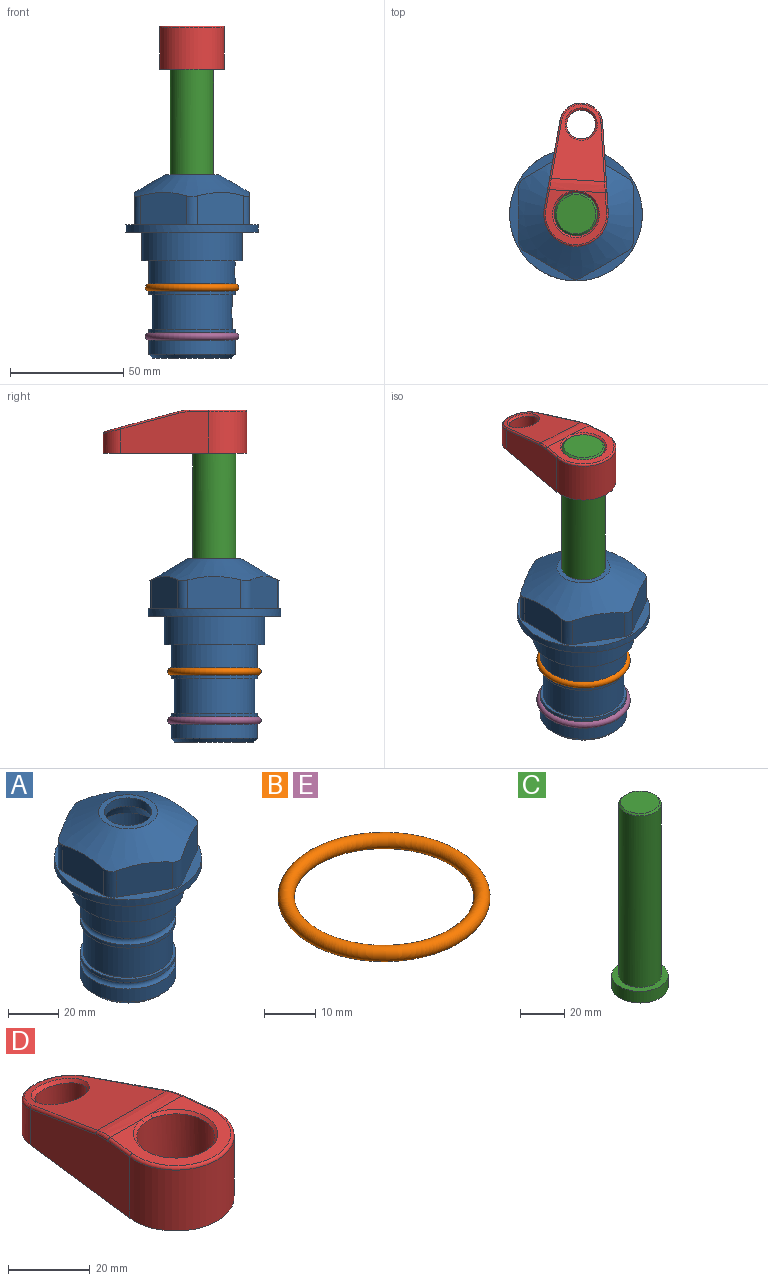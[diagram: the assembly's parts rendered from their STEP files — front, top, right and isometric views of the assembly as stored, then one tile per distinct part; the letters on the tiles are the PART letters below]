
ASSEMBLY  parts=5 mates=4
PART A: 36 faces, bbox 58.7x58.7x81 mm
  f0: cylinder r=17.78mm len=35.56mm, axis (0,0,1), area 1670.8mm2, adj f23,f24,f31
  f1: cylinder r=19.05mm len=38.1mm, axis (0,0,1), area 1191.9mm2, adj f26,f27,f30
  f2: plane 58.66x58.66mm, normal (0,0,-1), area 1150.6mm2, adj f3,f28
  f3: cylinder r=29.33mm len=58.66mm, axis (0,0,-1), area 585.1mm2, adj f2,f4
  f4: plane 58.66x58.66mm, normal (0,0,1), area 475.9mm2, adj f3,f5,f6,f7,f8,f9,f10,f11
  f5: plane 20.32x14.34mm, normal (-0.5,0.87,0), area 324.4mm2, adj f4,f15,f16,f17
  f6: plane 20.32x14.34mm, normal (0.5,0.87,0), area 324.4mm2, adj f4,f14,f15,f17
  f7: plane 23.48x14.34mm, normal (1,0,0), area 324.4mm2, adj f4,f13,f14,f17
  f8: plane 20.32x14.34mm, normal (0.5,-0.87,0), area 324.4mm2, adj f4,f12,f13,f17
  f9: plane 20.32x14.34mm, normal (-0.5,-0.87,0), area 324.4mm2, adj f4,f11,f12,f17
  f10: plane 23.48x14.34mm, normal (-1,0,0), area 324.4mm2, adj f4,f11,f16,f17
  f11: cylinder r=5.08mm len=12.85mm, axis (0,0,-1), area 67.2mm2, adj f4,f9,f10,f17
  f12: cylinder r=5.08mm len=12.85mm, axis (0,0,-1), area 67.2mm2, adj f4,f8,f9,f17
  f13: cylinder r=5.08mm len=12.85mm, axis (0,0,-1), area 67.2mm2, adj f4,f7,f8,f17
  f14: cylinder r=5.08mm len=12.85mm, axis (0,0,-1), area 67.2mm2, adj f4,f6,f7,f17
  f15: cylinder r=5.08mm len=12.85mm, axis (0,0,-1), area 67.2mm2, adj f4,f5,f6,f17
  f16: cylinder r=5.08mm len=12.85mm, axis (0,0,-1), area 67.2mm2, adj f4,f5,f10,f17
  f17: cone r=11.73mm half-angle=60deg, axis (0,0,-1), area 2071.8mm2, adj f5,f6,f7,f8,f9,f10,f11,f12
  f18: plane 23.46x23.46mm, normal (0,0,1), area 147.4mm2, adj f17,f35
  f19: plane 34.93x34.93mm, normal (0,0,-1), area 958mm2, adj f29
  f20: cylinder r=19.05mm len=38.1mm, axis (0,0,1), area 760.1mm2, adj f21,f29
  f21: torus R=19.05mm, axis (0,0,1), area 565.3mm2, adj f20,f22
  f22: cylinder r=19.05mm len=38.1mm, axis (0,0,1), area 190mm2, adj f21,f23
  f23: plane 38.1x38.1mm, normal (0,0,1), area 146.9mm2, adj f0,f22
  f24: plane 38.1x38.1mm, normal (0,0,-1), area 146.9mm2, adj f0,f25
  f25: cylinder r=19.05mm len=38.1mm, axis (0,0,1), area 190mm2, adj f24,f26
  f26: torus R=19.05mm, axis (0,0,1), area 565.3mm2, adj f1,f25
  f27: plane 44.45x44.45mm, normal (0,0,-1), area 411.7mm2, adj f1,f28
  f28: cylinder r=22.23mm len=44.45mm, axis (0,0,1), area 1773.5mm2, adj f2,f27
  f29: cone r=19.05mm half-angle=45deg, axis (0,0,1), area 257.5mm2, adj f19,f20
  f30: cylinder r=3.17mm len=6.75mm, axis (-1,0,0), area 128mm2, adj f1,f33
  f31: cylinder r=3.17mm len=6.35mm, axis (-1,0,0), area 102.5mm2, adj f0,f33
  f32: plane 25.4x25.4mm, normal (0,0,1), area 506.7mm2, adj f33
  f33: cylinder r=12.7mm len=66.42mm, axis (0,0,-1), area 5236.2mm2, adj f30,f31,f32,f34
  f34: cone r=9.53mm half-angle=30deg, axis (0,0,-1), area 443.4mm2, adj f33,f35
  f35: cylinder r=9.53mm len=19.05mm, axis (0,0,-1), area 240.9mm2, adj f18,f34
PART B: 1 faces, bbox 44.7x44.7x3.2 mm
  f0: torus R=19.05mm, axis (0,0,1), area 1193.9mm2
PART C: 6 faces, bbox 25.4x25.4x101.6 mm
  f0: plane 17.46x17.46mm, normal (0,0,1), area 239.5mm2, adj f5
  f1: plane 25.4x25.4mm, normal (0,0,-1), area 506.7mm2, adj f2
  f2: cylinder r=12.7mm len=25.4mm, axis (0,0,1), area 506.7mm2, adj f1,f3
  f3: plane 25.4x25.4mm, normal (0,0,1), area 221.7mm2, adj f2,f4
  f4: cylinder r=9.53mm len=94.46mm, axis (0,0,1), area 5653mm2, adj f3,f5
  f5: cone r=8.73mm half-angle=45deg, axis (0,0,-1), area 64.4mm2, adj f0,f4
PART D: 31 faces, bbox 31.7x65.5x19.8 mm
  f0: plane 39.12x18.26mm, normal (0.99,0.12,0), area 612.2mm2, adj f1,f4,f7,f11,f13,f15
  f1: cylinder r=9.53mm len=18.91mm, axis (0,0,-1), area 296.1mm2, adj f0,f2,f7,f17
  f2: plane 39.12x18.26mm, normal (-0.99,0.12,0), area 612.2mm2, adj f1,f4,f7,f12,f14,f16
  f3: cylinder r=6.35mm len=12.7mm, axis (0,0,-1), area 362.4mm2, adj f7,f18
  f4: cylinder r=14.29mm len=28.58mm, axis (0,0,-1), area 882.2mm2, adj f0,f2,f7,f10
  f5: cylinder r=9.53mm len=19.05mm, axis (0,0,-1), area 1092.6mm2, adj f7,f19,f20
  f6: plane 26.99x23.69mm, normal (0,0,1), area 216.2mm2, adj f9,f10,f11,f12,f19
  f7: plane 63.5x28.58mm, normal (0,0,-1), area 661.8mm2, adj f0,f1,f2,f3,f4,f5,f22,f23
  f8: plane 33.52x23.6mm, normal (0,0.26,0.97), area 486mm2, adj f9,f15,f16,f17,f18
  f9: cylinder r=19.05mm len=24.72mm, axis (1,0,0), area 120.4mm2, adj f6,f8,f13,f14,f20
  f10: torus R=13.49mm, axis (0,0,1), area 59mm2, adj f4,f6,f11,f12
  f11: cylinder r=0.79mm len=8.67mm, axis (0.12,-0.99,0), area 10.8mm2, adj f0,f6,f10,f13
  f12: cylinder r=0.79mm len=8.67mm, axis (0.12,0.99,0), area 10.8mm2, adj f2,f6,f10,f14
  f13: bspline ~4.95x1.42mm, area 6.1mm2, adj f0,f9,f11,f15
  f14: bspline ~4.95x1.42mm, area 6.1mm2, adj f2,f9,f12,f16
  f15: cylinder r=0.79mm len=25.95mm, axis (0.12,-0.96,0.26), area 32.9mm2, adj f0,f8,f13,f17
  f16: cylinder r=0.79mm len=25.95mm, axis (0.12,0.96,-0.26), area 32.9mm2, adj f2,f8,f14,f17
  f17: bspline ~18.91x8.38mm, area 30mm2, adj f1,f8,f15,f16
  f18: bspline ~14.29x14.29mm, area 48.3mm2, adj f3,f8
  f19: cone r=9.53mm half-angle=45deg, axis (0,0,1), area 66.5mm2, adj f5,f6,f20
  f20: bspline ~3.22x0.96mm, area 3.5mm2, adj f5,f9,f19
  f21: plane 2.75x2.72mm, normal (0,0,-1), area 2.9mm2, adj f23,f25,f28
  f22: plane 23.05x15.88mm, normal (-0.99,-0.12,0), area 323.6mm2, adj f7,f25,f26,f27,f28,f29
  f23: plane 23.05x15.88mm, normal (0.99,-0.12,0), area 323.6mm2, adj f7,f21,f25,f27,f28,f30
  f24: cylinder r=9.53mm len=10.69mm, axis (0,0,-1), area 114.7mm2, adj f7,f27,f29,f30
  f25: cylinder r=12.7mm len=20.59mm, axis (0,0,-1), area 381.1mm2, adj f7,f21,f22,f23,f26,f28
  f26: plane 2.75x2.72mm, normal (0,0,-1), area 2.9mm2, adj f22,f25,f28
  f27: plane 19.72x18.37mm, normal (0,-0.26,-0.97), area 291.8mm2, adj f22,f23,f24,f28,f29,f30
  f28: cylinder r=15.88mm len=19.92mm, axis (1,0,0), area 54.8mm2, adj f21,f22,f23,f25,f26,f27
  f29: cylinder r=1.59mm len=11mm, axis (0,0,-1), area 34.7mm2, adj f7,f22,f24,f27
  f30: cylinder r=1.59mm len=11mm, axis (0,0,-1), area 34.7mm2, adj f7,f23,f24,f27
PART E: same geometry as B
PLACE A t=(-14.58,-13.88,2.73)mm fixed
PLACE B t=(-14.58,-13.88,2.73)mm
PLACE C rot(axis=(0,0,-1),3.3deg) t=(-14.58,-13.88,30.29)mm
PLACE D rot(axis=(0,0,-1),3.3deg) t=(-14.58,-13.88,30.29)mm
PLACE E t=(-14.58,-13.88,-18.86)mm
MATE fastened E.f0 <-> A.f0  axis (0,0,1) through (-14.58,-13.88,-43.37)mm
MATE fastened C.f2 <-> D.f4  axis (0,0,-1) through (-14.58,-13.88,92.99)mm
MATE fastened B.f0 <-> A.f0  axis (0,0,1) through (-14.58,-13.88,-21.78)mm
MATE cylindrical C.f2 <-> A.f0  axis (0,0,-1) through (-14.58,-13.88,-7.81)mm
